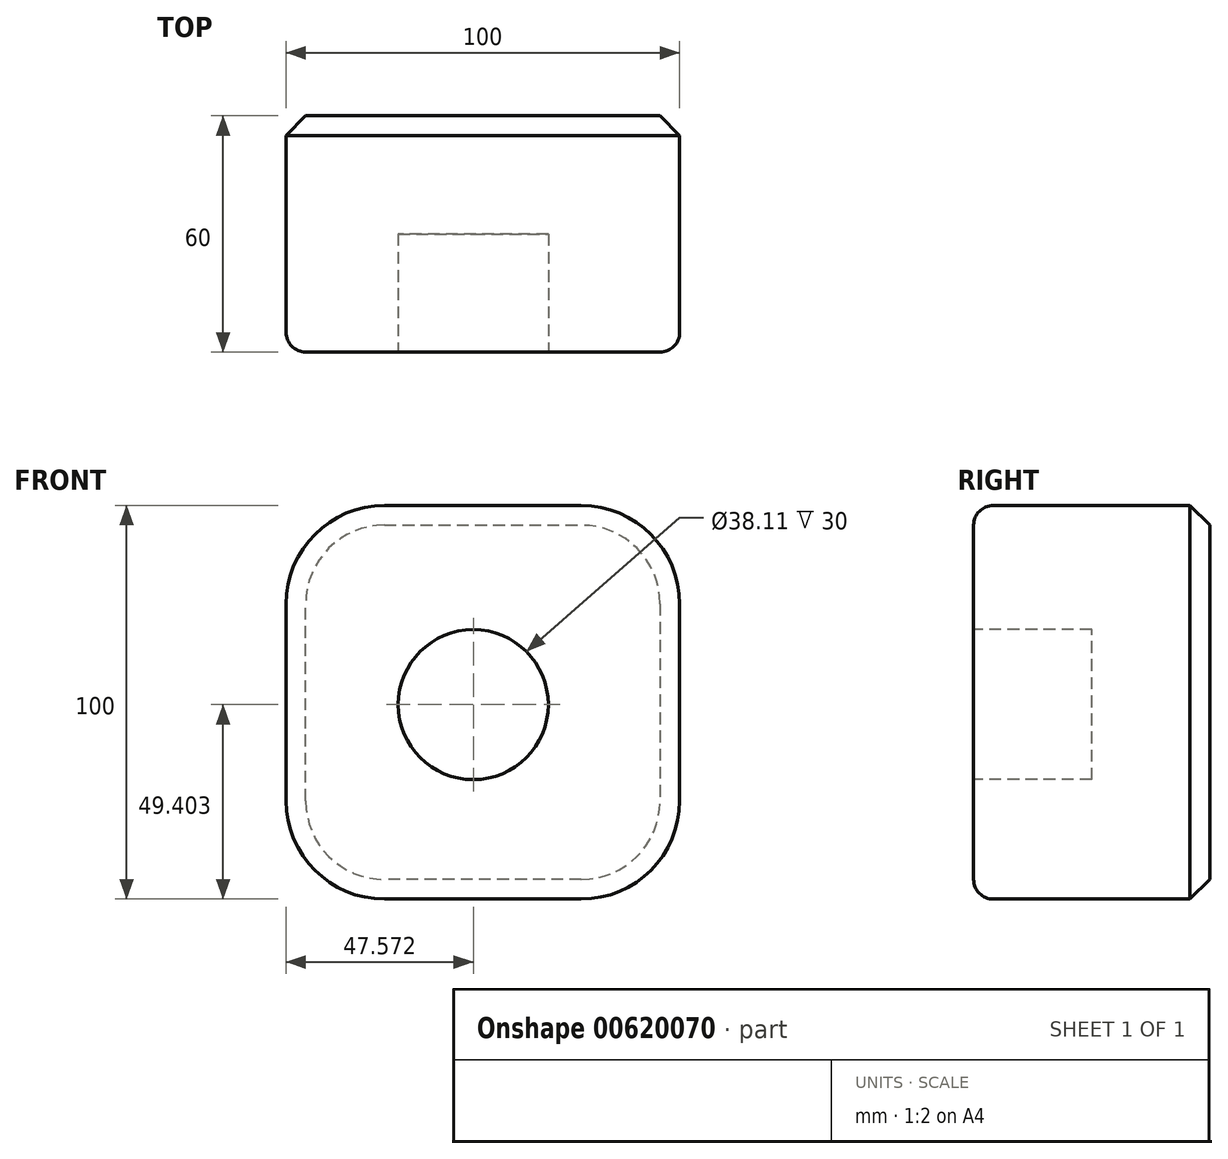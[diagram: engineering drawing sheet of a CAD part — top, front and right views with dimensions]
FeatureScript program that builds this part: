
annotation { "Feature Type Name" : "Feature", "Feature Type Description" : "" }
export const myFeature = defineFeature(function(context is Context, id is Id, definition is map)
    precondition{}
    {
        {
            var Q0;
            Q0=qCreatedBy(makeId("Front.planeOp"),FACE);
            var sketch = newSketch(context, id + "F0", { "sketchPlane" : qUnion([Q0])});
            skLineSegment(sketch, "E0.bottom", {"start": v(-13.44, 58.78) * mm, "end": v(36.56, 58.78) * mm});
            skLineSegment(sketch, "E0.top", {"start": v(-13.44, -41.22) * mm, "end": v(36.56, -41.22) * mm});
            skLineSegment(sketch, "E0.left", {"start": v(-38.44, 33.78) * mm, "end": v(-38.44, -16.22) * mm});
            skLineSegment(sketch, "E0.right", {"start": v(61.56, 33.78) * mm, "end": v(61.56, -16.22) * mm});
            skPoint(sketch, "E1.visualSharp", {"position": v(-38.44, 58.78) * mm});
            skArc(sketch, "E1.filletArc", {"start": v(-13.44, 58.78) * mm, "mid": v(-31.12, 51.45) * mm, "end": v(-38.44, 33.78) * mm});
            skPoint(sketch, "E2.visualSharp", {"position": v(61.56, 58.78) * mm});
            skArc(sketch, "E2.filletArc", {"start": v(61.56, 33.78) * mm, "mid": v(54.24, 51.45) * mm, "end": v(36.56, 58.78) * mm});
            skPoint(sketch, "E3.visualSharp", {"position": v(61.56, -41.22) * mm});
            skArc(sketch, "E3.filletArc", {"start": v(36.56, -41.22) * mm, "mid": v(54.24, -33.9) * mm, "end": v(61.56, -16.22) * mm});
            skPoint(sketch, "E4.visualSharp", {"position": v(-38.44, -41.22) * mm});
            skArc(sketch, "E4.filletArc", {"start": v(-38.44, -16.22) * mm, "mid": v(-31.12, -33.9) * mm, "end": v(-13.44, -41.22) * mm});
            skSolve(sketch);
        }
        {
            var Q0;
            Q0 = qSketchRegion(id + "F0", true);
            extrude(context, id + "F1", {"entities" : qUnion([Q0]), "depth" : 60 * mm, "offsetDistance" : 25 * mm});
        }
        {
            var Q0;
            Q0=makeQuery(id+"F1.opExtrude","CAP_FACE",FACE,{"disambiguationData":[OSD([sQuery(id+"F0.wireOp",EDGE,"E0.bottom"),sQuery(id+"F0.wireOp",EDGE,"E0.top"),sQuery(id+"F0.wireOp",EDGE,"E0.left"),sQuery(id+"F0.wireOp",EDGE,"E0.right"),sQuery(id+"F0.wireOp",EDGE,"E1.filletArc"),sQuery(id+"F0.wireOp",EDGE,"E2.filletArc"),sQuery(id+"F0.wireOp",EDGE,"E3.filletArc"),sQuery(id+"F0.wireOp",EDGE,"E4.filletArc")])],"isStart":false});
            fillet(context, id + "F2", {"entities" : qUnion([Q0]), "radius" : 5 * mm, "tangentPropagation" : true, "allowEdgeOverflow" : false});
        }
        {
            var Q0;
            Q0=makeQuery(id+"F1.opExtrude","CAP_FACE",FACE,{"disambiguationData":[OSD([sQuery(id+"F0.wireOp",EDGE,"E0.bottom"),sQuery(id+"F0.wireOp",EDGE,"E0.top"),sQuery(id+"F0.wireOp",EDGE,"E0.left"),sQuery(id+"F0.wireOp",EDGE,"E0.right"),sQuery(id+"F0.wireOp",EDGE,"E1.filletArc"),sQuery(id+"F0.wireOp",EDGE,"E2.filletArc"),sQuery(id+"F0.wireOp",EDGE,"E3.filletArc"),sQuery(id+"F0.wireOp",EDGE,"E4.filletArc")])],"isStart":true});
            chamfer(context, id + "F3", {"entities" : qUnion([Q0]), "width" : 5 * mm, "tangentPropagation" : true});
        }
        {
            var Q0;
            Q0=makeQuery(id+"F1.opExtrude","CAP_FACE",FACE,{"disambiguationData":[OSD([sQuery(id+"F0.wireOp",EDGE,"E0.bottom"),sQuery(id+"F0.wireOp",EDGE,"E0.top"),sQuery(id+"F0.wireOp",EDGE,"E0.left"),sQuery(id+"F0.wireOp",EDGE,"E0.right"),sQuery(id+"F0.wireOp",EDGE,"E1.filletArc"),sQuery(id+"F0.wireOp",EDGE,"E2.filletArc"),sQuery(id+"F0.wireOp",EDGE,"E3.filletArc"),sQuery(id+"F0.wireOp",EDGE,"E4.filletArc")])],"isStart":false});
            var sketch = newSketch(context, id + "F4", { "sketchPlane" : qUnion([Q0])});
            skCircle(sketch, "E5", {"center": v(9.13, 8.18) * mm, "radius": 19.05 * mm});
            skSolve(sketch);
        }
        {
            var Q0;
            Q0=makeQuery(id+"F4.imprint","IMPRINT",FACE,{"disambiguationData":[TD([[makeQuery(id+"F4.imprint","IMPRINT",EDGE,{"derivedFrom":sQuery(id+"F4.wireOp",EDGE,"E5")}),1.0]])]});
            extrude(context, id + "F5", {"entities" : qUnion([Q0]), "operationType" : NewBodyOperationType.REMOVE, "oppositeDirection" : true, "depth" : 30 * mm, "offsetDistance" : 25 * mm});
        }
    });
